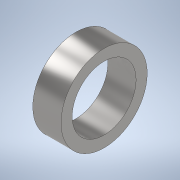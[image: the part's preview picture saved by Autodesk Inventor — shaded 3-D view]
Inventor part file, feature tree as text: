
AUTODESK INVENTOR PART (.ipt)
format: ipt  version: 2022.1 (Build 261234000, 234)  size: 107,520 bytes
history: native  units: in
note: dims shown in document units (in); Inventor stores cm internally (conversion verified against a paired STEP export)
features: other x1, extrude x1, sketch x1
ambient origin geometry x8: Origin, YZ Plane, XZ Plane, XY Plane, X Axis, Y Axis, Z Axis, Center Point
bodies: Body1 (feature_tree)
feature tree (3):
  other  "Sólido1"
  extrude  "Extrusión1"  Depth=0.7998in
  sketch  "Boceto1"  dims[d0=1.811in d1=2.4409in d2=0.7998in d3=0.0in d4=0.0197in d5=0.0344in]
